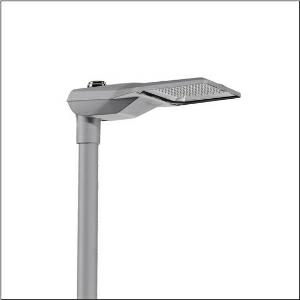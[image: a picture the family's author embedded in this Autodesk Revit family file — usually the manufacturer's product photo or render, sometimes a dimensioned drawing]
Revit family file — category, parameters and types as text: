
# Revit family: streetlight_sl_21_midi___p0_8a_5xe7u57n08mb_b7af
name_source: partatom
category: Lighting Fixtures
units: mm (PartAtom-declared; Revit-internal decimal feet)

## family parameters
Cut with Voids When Loaded = No
Host = Face
Light Source = No
Part Type = Normal
Room Calculation Point = No
Round Connector Dimension = Use Diameter
Shared = No

## types (1)
- --- (1 x LED, 15940 lm, 137 W, 3000K)
    Apparent Load = 137 VA
    CIE Flux Codes = 33 69 96 100 100
    Color Rendering = 80
    Color Temperature = 3000K
    Default Elevation = 1800 mm
    Description = Streetlight SL 21 midi, mast luminaire, primary light control with lens, of PMMA, primary optical cover: cover, of toughened safety glass, transparent, light distribution: P0.8a, light emission: direct distribution, primary light characteristic: asymmetric, installation type: side-entry, LED, 3G 2.5mm², High Power LED, rated luminous flux: 15.940lm, luminous efficacy: 116lm/W, light colour: 830, colour temperature: 3000K, control gear: NEMA (7pin), control: flexible luminous flux parameterisation, time-dependent luminous flux control, constant luminous flux control, pre-setting: linear dimming characteristic, overheat protection, mains connection: 220..240V, AC, 50/60Hz, connection cable pre-assembled, cable length: 12,5m, wiring characteristics: H05VV-F, start of lifetime: 137W, end of service life: 144W, reduction: 61W, luminaire housing, of diecast aluminium (EN AC-44300), powder-coated, Siteco® metallic grey (DB 702S), corrosivity category C5 mid according to DIN EN ISO 12944, multi-level sealing system, sealing non-destructively replaceable, inclination adjustable: 0°, 5°, 10°, 15°, length: 644mm, width: 335mm, height: 110mm, spigot size: 42mm (side-entry), mounting height: 4..8m, protection rating (complete): IP66, insulation class (complete): insulation class I (protective earthing), certification: CE, ENEC, ENEC+, VDE, impact resistance: IK09, permissible operating ambient temperature for outdoor applications: -40..+50°C, standard-compliant lighting for roads and squares, packaging unit: 1 piece

Light Distribution: P0.8a
    Height = 111 mm
    Lamp = 1 x LED
    Lamp Light Flux = 15940 lm
    Lamp Power = 137 W
    Lamp count = 1
    Length = 644 mm
    Luminous efficacy = 116 lm/W
    Manufacturer = Siteco
    ModVariant = No
    Model = 5XE7U57N08MB
    Number of Poles = 1
    OnlyDefault = Yes
    Power Factor = 1
    Product Name = Streetlight SL 21 midi | P0.8a
    Product group = mast luminaire | pylon top
    ProductGroupID = 6100
    Protection Class = Protection class I
    Protection Degree = IP 66
    RLX_Detail_Level = 1
    RLX_Emergency_Light_Flux = 0 lm
    RLX_Emergency_Type = 0
    RLX_Emergency_Type_DB = No
    RlxData = <blob elided: 89965 chars, md5=c15962d5>
    Socket = socket
    Standby Power = 0 W
    System Light Flux = 15940 lm
    System Power = 137 W
    Type Comments = factory setting: luminous flux: 100 % | dim-lin: 254 | 700 mA
    Type Image = l_1294377.jpg
    URL = http://relux.com
    VarID = @adj_070198
    Voltage = 0 V
    Weight = 0.00 kg
    Width = 336 mm

## geometry (parser evidence)
native form markers: Blend x4, Sweep x10
no freeform markers — native parametric forms only
